# Revit family: NLRS_57_AIR_UN_design-penthouse-louvre-bdhn-fresh-air_LT_sacs
name_source: partatom
category: Air Terminals
units: mm (PartAtom-declared; Revit-internal decimal feet)

## family parameters
Always vertical = Yes
Cut with Voids When Loaded = No
Part Type = Normal
Room Calculation Point = No
Round Connector Dimension = Use Diameter
Shared = No
Work Plane-Based = No

## types (4) — shared parameters
Assembly Code = 57.00
Default Elevation = 200 mm  [stored 0.656168 ft]
Description = Compacte Design aluminium dakkap BDHN (aanzuig)
Manufacturer = Solid Air Climate Solutions
Model = BDHN
NLRS_C_content_datum_gewijzigd = 17-07-2025
NLRS_C_content_provider = Solid Air Climate Solutions
NLRS_C_content_versie = 1.22.01
NLRS_C_description = Compacte Design aluminium dakkap BDHN (aanzuig)
SACS_Data_Hidden = BDHN
Type Comments = Width x Length = aansluitmaat!
URL = https://solid-air.nl

## per-type parameters (varying)
| type | SACS_Base_Index | SACS_Index3 | SACS_Index4 |
| BDHNGO | 0 | 0 mm  [stored 0 ft] | 0 mm  [stored 0 ft] |
| BDHNSO | 1 | 1 mm  [stored 0.00328084 ft] | 0 mm  [stored 0 ft] |
| BDHNGB | 2 | 0 mm  [stored 0 ft] | 1 mm  [stored 0.00328084 ft] |
| BDHNSB | 3 | 1 mm  [stored 0.00328084 ft] | 1 mm  [stored 0.00328084 ft] |

note: [stored X ft] marks values corroborated as IEEE doubles in the binary element streams (Revit-internal decimal feet)

## geometry (parser evidence)
native form markers: Sweep x17
no freeform markers — native parametric forms only
